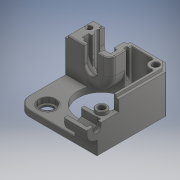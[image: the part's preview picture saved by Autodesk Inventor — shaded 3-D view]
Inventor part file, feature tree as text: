
AUTODESK INVENTOR PART (.ipt)
format: ipt  version: 2017 (Build 210142000, 142)  size: 1,039,360 bytes
history: native  units: in
note: dims shown in document units (in); Inventor stores cm internally (conversion verified against a paired STEP export)
features: extrude x35, sketch x35, projected_geometry x24, fillet x7, chamfer x3, pattern_circular x1
ambient origin geometry x8: Origin, YZ Plane, XZ Plane, XY Plane, X Axis, Y Axis, Z Axis, Center Point
bodies: Solid1 (feature_tree)
feature tree (105):
  extrude  "Extrusion1"  Depth=1.811in
  fillet  "Fillet1"  Radius=1.7323in
  extrude  "Extrusion2"  Depth=0.815in
  extrude  "Extrusion3"  Depth=0.2953in
  extrude  "Extrusion4"  Depth=1.2205in
  fillet  "Fillet2"  Radius=0.1437in
  extrude  "Extrusion5"  Depth=0.1437in
  fillet  "Fillet3"  Radius=0.2638in
  pattern_circular  "Circular Pattern1"  Count=10 Angle=360.0deg
  extrude  "Extrusion6"  Depth=0.1181in
  extrude  "Extrusion7"  Depth=0.6299in
  extrude  "Extrusion8"  Depth=0.7835in TaperAngle=0.0deg
  extrude  "Extrusion9"  TaperAngle=0.0deg  [1 undecoded]
  extrude  "Extrusion10"  Depth=1.2402in
  extrude  "Extrusion11"  Depth=0.1831in
  extrude  "Extrusion12"  Depth=0.0689in TaperAngle=0.0deg
  extrude  "Extrusion13"  Depth=0.0787in TaperAngle=0.0deg
  extrude  "Extrusion14"  Depth=0.0787in TaperAngle=0.0deg
  extrude  "Extrusion15"  Depth=0.0591in
  extrude  "Extrusion16"  Depth=0.2441in
  extrude  "Extrusion17"  TaperAngle=0.0deg  [1 undecoded]
  extrude  "Extrusion18"  Depth=0.5551in
  extrude  "Extrusion19"  Depth=0.6378in
  extrude  "Extrusion20"  Depth=0.5354in
  extrude  "Extrusion21"  Depth=0.2303in TaperAngle=0.0deg
  extrude  "Extrusion22"  Depth=0.0709in
  chamfer  "Chamfer1"  Distance=0.0492in
  extrude  "Extrusion23"  Depth=0.0492in TaperAngle=0.0deg
  extrude  "Extrusion24"  Depth=0.0492in TaperAngle=0.0deg
  extrude  "Extrusion25"  Depth=0.0787in TaperAngle=0.0deg
  fillet  "Fillet4"  Radius=0.0591in
  chamfer  "Chamfer2"  Distance=0.0591in
  extrude  "Extrusion26"  Depth=0.0787in
  fillet  "Fillet6"  Radius=0.5512in
  fillet  "Fillet7"  Radius=0.0591in
  fillet  "Fillet8"  Radius=0.0492in
  extrude  "Extrusion27"  Depth=0.0787in TaperAngle=0.0deg
  extrude  "Extrusion28"  Depth=0.0787in TaperAngle=0.0deg
  extrude  "Extrusion29"  Depth=0.0787in
  extrude  "Extrusion30"  Depth=0.0787in TaperAngle=45.0deg
  extrude  "Extrusion31"  Depth=0.0591in
  extrude  "Extrusion32"  Depth=0.0591in
  extrude  "Extrusion33"  Depth=0.0591in
  extrude  "Extrusion34"  Depth=0.0591in
  extrude  "Extrusion35"  Depth=0.0591in TaperAngle=0.0deg
  chamfer  "Chamfer3"  Distance=0.0394in
  sketch  "Sketch1"  dims[d0=1.063in d1=1.811in d2=1.7323in]
  sketch  "Sketch2"  dims[d3=0.815in d4=0.815in]
  sketch  "Sketch3"  dims[d5=0.1378in d6=0.0in d7=0.2953in]
  projected_geometry  "Projected Loop1"
  sketch  "Sketch4"  dims[d8=1.2205in d9=1.2205in d10=0.1437in]
  projected_geometry  "Projected Loop2"
  sketch  "Sketch5"  dims[d11=0.1437in d12=0.1437in d13=0.2638in]
  projected_geometry  "Projected Loop3"
  sketch  "Sketch7"  dims[d14=0.1378in d15=0.0in]
  projected_geometry  "Projected Loop4"
  sketch  "Sketch8"  dims[d16=0.3622in]
  sketch  "Sketch9"  dims[d17=0.0984in d18=0.0in]
  sketch  "Sketch10"  dims[d19=0.4173in]
  sketch  "Sketch11"  dims[d20=0.0138in d21=0.0in]
  projected_geometry  "Projected Loop5"
  sketch  "Sketch13"  dims[d22=0.0138in]
  projected_geometry  "Projected Loop7"
  sketch  "Sketch14"  dims[d23=0.0118in]
  projected_geometry  "Projected Loop8"
  sketch  "Sketch15"  dims[d24=0.1752in]
  sketch  "Sketch16"  dims[d25=0.0138in d26=0.0in]
  projected_geometry  "Projected Loop9"
  sketch  "Sketch17"  dims[d27=0.0059in d28=3.937in d29=360.0deg]
  projected_geometry  "Projected Loop10"
  sketch  "Sketch18"  dims[d31=0.5118in d33=0.1181in]
  projected_geometry  "Projected Loop11"
  sketch  "Sketch19"  dims[d34=0.9843in d35=0.6299in]
  projected_geometry  "Projected Loop12"
  sketch  "Sketch21"  dims[d36=0.1181in d37=0.7835in d38=0.0in]
  sketch  "Sketch22"  dims[d42=0.5354in d43=0.0in d44=0.0in]
  projected_geometry  "Projected Loop14"
  sketch  "Sketch23"  dims[d46=0.6102in d47=1.2402in]
  projected_geometry  "Projected Loop15"
  sketch  "Sketch24"  dims[d48=0.9213in d49=0.0in d50=0.1831in]
  sketch  "Sketch25"  dims[d51=0.0915in d52=0.0689in d53=0.0in]
  projected_geometry  "Projected Loop16"
  sketch  "Sketch26"  dims[d54=0.315in d55=0.0787in d56=0.0in]
  projected_geometry  "Projected Loop17"
  sketch  "Sketch27"  dims[d57=0.2972in d58=0.0787in d59=0.0in]
  projected_geometry  "Projected Loop18"
  sketch  "Sketch28"  dims[d60=0.0591in d62=0.0394in]
  projected_geometry  "Projected Loop19"
  sketch  "Sketch29"  dims[d63=0.0669in d64=0.0in d65=0.2441in]
  projected_geometry  "Projected Loop20"
  projected_geometry  "Projected Loop21"
  sketch  "Sketch30"  dims[d66=0.5551in d67=0.0in]
  sketch  "Sketch31"  dims[d68=0.0689in d69=0.5551in]
  sketch  "Sketch32"  dims[d70=0.0in d72=0.6378in]
  projected_geometry  "Projected Loop22"
  sketch  "Sketch33"  dims[d73=0.248in d74=0.5354in]
  projected_geometry  "Projected Loop23"
  sketch  "Sketch34"  dims[d75=0.124in d76=0.0in d78=0.2303in d79=0.0in]
  sketch  "Sketch35"  dims[d80=0.1496in d81=0.0in d82=0.0709in d83=0.0492in d84=0.0in]
  sketch  "Sketch36"  dims[d85=0.2953in d86=0.0492in d87=0.0in]
  projected_geometry  "Projected Loop24"
  sketch  "Sketch37"  dims[d88=0.2362in d89=0.0492in d90=0.0in]
  projected_geometry  "Projected Loop25"
  sketch  "Sketch38"  dims[d91=0.2362in d92=0.0492in d93=0.0in d94=0.0591in d95=0.0591in d97=0.0728in d98=0.5512in d99=0.0in d100=0.0591in d101=0.0787in d102=45.0deg d103=0.0492in d104=0.0in d105=0.0492in d106=0.0in d107=0.0079in d108=0.0in d109=0.1378in d110=0.1772in d111=0.0787in d112=45.0deg d113=0.0591in d114=0.0591in d115=0.0591in d116=0.0591in d117=0.0591in d118=0.0in d120=0.0394in d121=0.0118in d122=0.0197in d123=0.3425in d124=0.0925in d125=0.0866in d126=0.0669in d127=0.3307in d128=0.0in d129=0.0551in d130=0.1575in d131=0.0787in d132=0.0531in d133=0.1575in d134=0.3445in d135=0.1575in d136=0.0in d137=0.5512in d138=0.1575in d139=0.0in d140=0.1575in d141=0.0in d142=0.0984in d143=0.0394in d144=0.1575in d145=0.0in d146=0.126in d147=0.2362in d148=0.1417in d149=0.0531in d150=0.1575in d151=0.0in d152=0.1575in d153=0.0in d154=0.2126in d155=0.0787in d156=0.0276in d157=0.0in d158=0.1575in d159=0.1181in d160=0.0in d161=0.863in d162=0.0236in d163=0.0787in d164=45.0deg]
  projected_geometry  "Projected Loop26"
note: 2 required parameter values undecoded (feature->parameter linkage not recoverable at this tier; creation-order binding heuristic only, values carry confidence <= 0.55)
